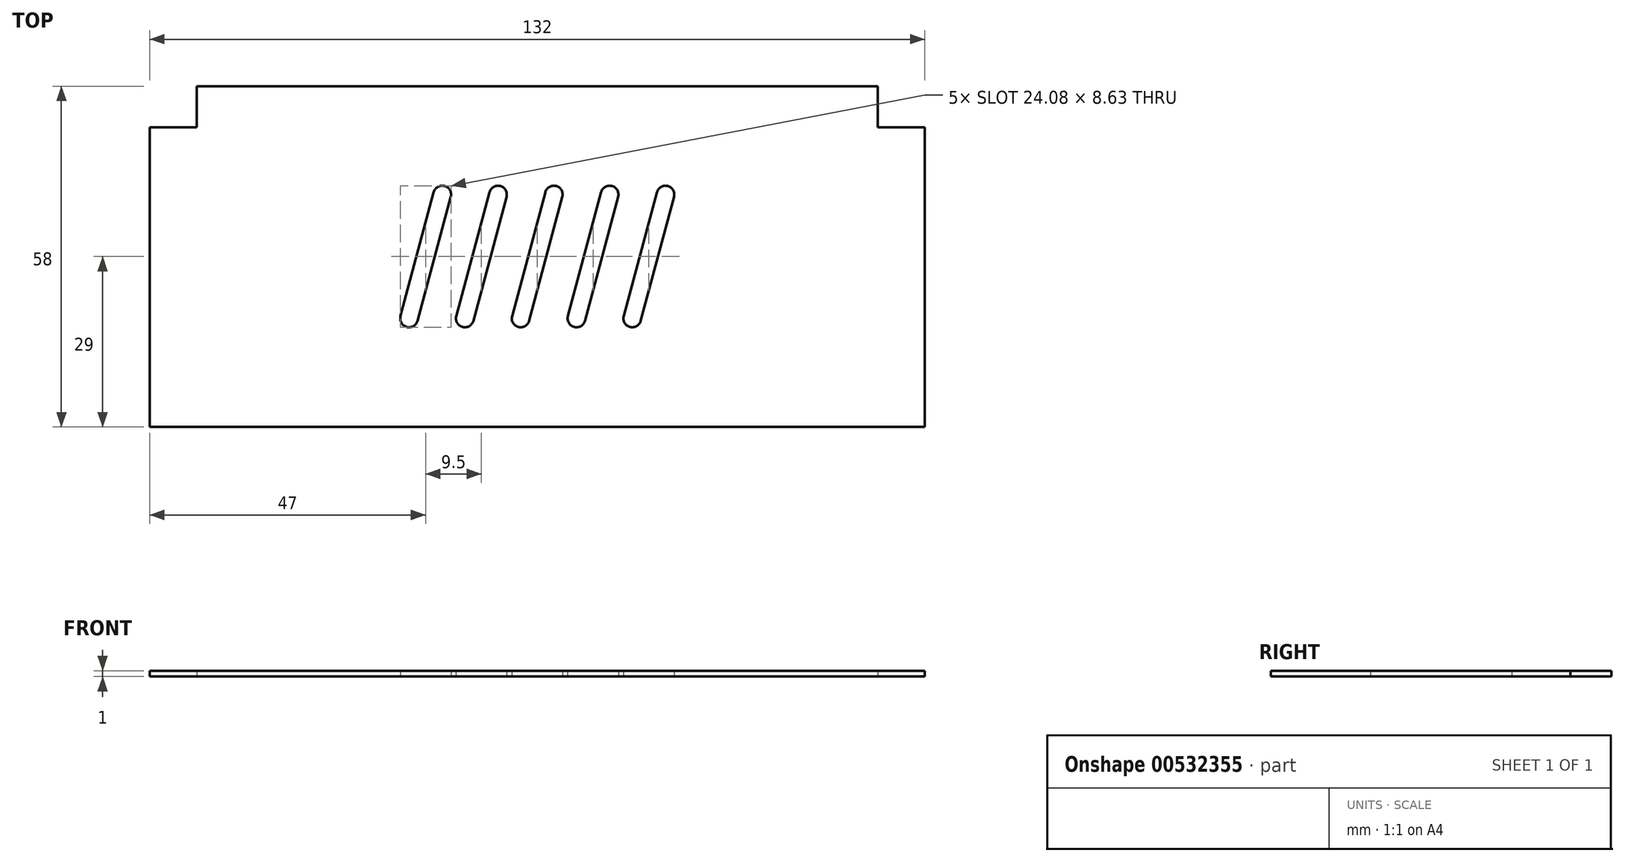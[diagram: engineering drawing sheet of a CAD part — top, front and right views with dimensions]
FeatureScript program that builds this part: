
annotation { "Feature Type Name" : "Feature", "Feature Type Description" : "" }
export const myFeature = defineFeature(function(context is Context, id is Id, definition is map)
    precondition{}
    {
        {
            var Q0;
            Q0=qCreatedBy(makeId("Top.planeOp"),FACE);
            var sketch = newSketch(context, id + "F0", { "sketchPlane" : qUnion([Q0])});
            skLineSegment(sketch, "E0.bottom", {"start": v(58, 29) * mm, "end": v(-58, 29) * mm});
            skLineSegment(sketch, "E0.top", {"start": v(66, -29) * mm, "end": v(-66, -29) * mm});
            skLineSegment(sketch, "E0.left", {"start": v(66, 22) * mm, "end": v(66, -29) * mm});
            skLineSegment(sketch, "E0.right", {"start": v(-66, 22) * mm, "end": v(-66, -29) * mm});
            skPoint(sketch, "E0.middle", {"position": v(0, 0) * mm});
            skLineSegment(sketch, "E1", {"start": v(-3.22, -12) * mm, "end": v(3.22, 12) * mm, "construction": true});
            skLineSegment(sketch, "E2.0", {"start": v(-1.38, -10.94) * mm, "end": v(4.28, 10.16) * mm});
            skLineSegment(sketch, "E3.0", {"start": v(-4.28, -10.16) * mm, "end": v(1.38, 10.94) * mm});
            skArc(sketch, "E4", {"start": v(4.28, 10.16) * mm, "mid": v(3.22, 12) * mm, "end": v(1.38, 10.94) * mm});
            skArc(sketch, "E5", {"start": v(-4.28, -10.16) * mm, "mid": v(-3.22, -12) * mm, "end": v(-1.38, -10.94) * mm});
            skLineSegment(sketch, "E6.1.0.0", {"start": v(5.22, -10.16) * mm, "end": v(10.88, 10.94) * mm});
            skLineSegment(sketch, "E6.1.0.1", {"start": v(6.28, -12) * mm, "end": v(12.72, 12) * mm, "construction": true});
            skLineSegment(sketch, "E6.1.0.2", {"start": v(8.12, -10.94) * mm, "end": v(13.78, 10.16) * mm});
            skPoint(sketch, "E6.1.0.3", {"position": v(9.5, 0) * mm});
            skPoint(sketch, "E6.1.0.4", {"position": v(9.5, 0) * mm});
            skArc(sketch, "E6.1.0.5", {"start": v(13.78, 10.16) * mm, "mid": v(12.72, 12) * mm, "end": v(10.88, 10.94) * mm});
            skArc(sketch, "E6.1.0.6", {"start": v(5.22, -10.16) * mm, "mid": v(6.28, -12) * mm, "end": v(8.12, -10.94) * mm});
            skLineSegment(sketch, "E6.2.0.0", {"start": v(14.72, -10.16) * mm, "end": v(20.38, 10.94) * mm});
            skLineSegment(sketch, "E6.2.0.1", {"start": v(15.78, -12) * mm, "end": v(22.22, 12) * mm, "construction": true});
            skLineSegment(sketch, "E6.2.0.2", {"start": v(17.62, -10.94) * mm, "end": v(23.28, 10.16) * mm});
            skPoint(sketch, "E6.2.0.3", {"position": v(19, 0) * mm});
            skPoint(sketch, "E6.2.0.4", {"position": v(19, 0) * mm});
            skArc(sketch, "E6.2.0.5", {"start": v(23.28, 10.16) * mm, "mid": v(22.22, 12) * mm, "end": v(20.38, 10.94) * mm});
            skArc(sketch, "E6.2.0.6", {"start": v(14.72, -10.16) * mm, "mid": v(15.78, -12) * mm, "end": v(17.62, -10.94) * mm});
            skLineSegment(sketch, "E6.direction1", {"start": v(-3.22, -12) * mm, "end": v(6.28, -12) * mm, "construction": true});
            skLineSegment(sketch, "E7.1.0.0", {"start": v(-12.72, -12) * mm, "end": v(-6.28, 12) * mm, "construction": true});
            skArc(sketch, "E7.1.0.1", {"start": v(-13.78, -10.16) * mm, "mid": v(-12.72, -12) * mm, "end": v(-10.88, -10.94) * mm});
            skLineSegment(sketch, "E7.1.0.2", {"start": v(-10.88, -10.94) * mm, "end": v(-5.22, 10.16) * mm});
            skLineSegment(sketch, "E7.1.0.3", {"start": v(-13.78, -10.16) * mm, "end": v(-8.12, 10.94) * mm});
            skArc(sketch, "E7.1.0.4", {"start": v(-5.22, 10.16) * mm, "mid": v(-6.28, 12) * mm, "end": v(-8.12, 10.94) * mm});
            skLineSegment(sketch, "E7.2.0.0", {"start": v(-22.22, -12) * mm, "end": v(-15.78, 12) * mm, "construction": true});
            skArc(sketch, "E7.2.0.1", {"start": v(-23.28, -10.16) * mm, "mid": v(-22.22, -12) * mm, "end": v(-20.38, -10.94) * mm});
            skLineSegment(sketch, "E7.2.0.2", {"start": v(-20.38, -10.94) * mm, "end": v(-14.72, 10.16) * mm});
            skLineSegment(sketch, "E7.2.0.3", {"start": v(-23.28, -10.16) * mm, "end": v(-17.62, 10.94) * mm});
            skArc(sketch, "E7.2.0.4", {"start": v(-14.72, 10.16) * mm, "mid": v(-15.78, 12) * mm, "end": v(-17.62, 10.94) * mm});
            skLineSegment(sketch, "E7.direction1", {"start": v(-3.22, -12) * mm, "end": v(-12.72, -12) * mm, "construction": true});
            skLineSegment(sketch, "E8.top", {"start": v(-66, 22) * mm, "end": v(-58, 22) * mm});
            skLineSegment(sketch, "E8.right", {"start": v(-58, 29) * mm, "end": v(-58, 22) * mm});
            skLineSegment(sketch, "E9.top", {"start": v(66, 22) * mm, "end": v(58, 22) * mm});
            skLineSegment(sketch, "E9.right", {"start": v(58, 29) * mm, "end": v(58, 22) * mm});
            skPoint(sketch, "E10.orphan", {"position": v(-66, 29) * mm});
            skPoint(sketch, "E11.orphan", {"position": v(66, 29) * mm});
            skSolve(sketch);
        }
        {
            var Q0;
            Q0=qSketchRegion(id+"F0",true);
            extrude(context, id + "F1", {"entities" : qUnion([Q0]), "depth" : 1 * mm});
        }
    });
